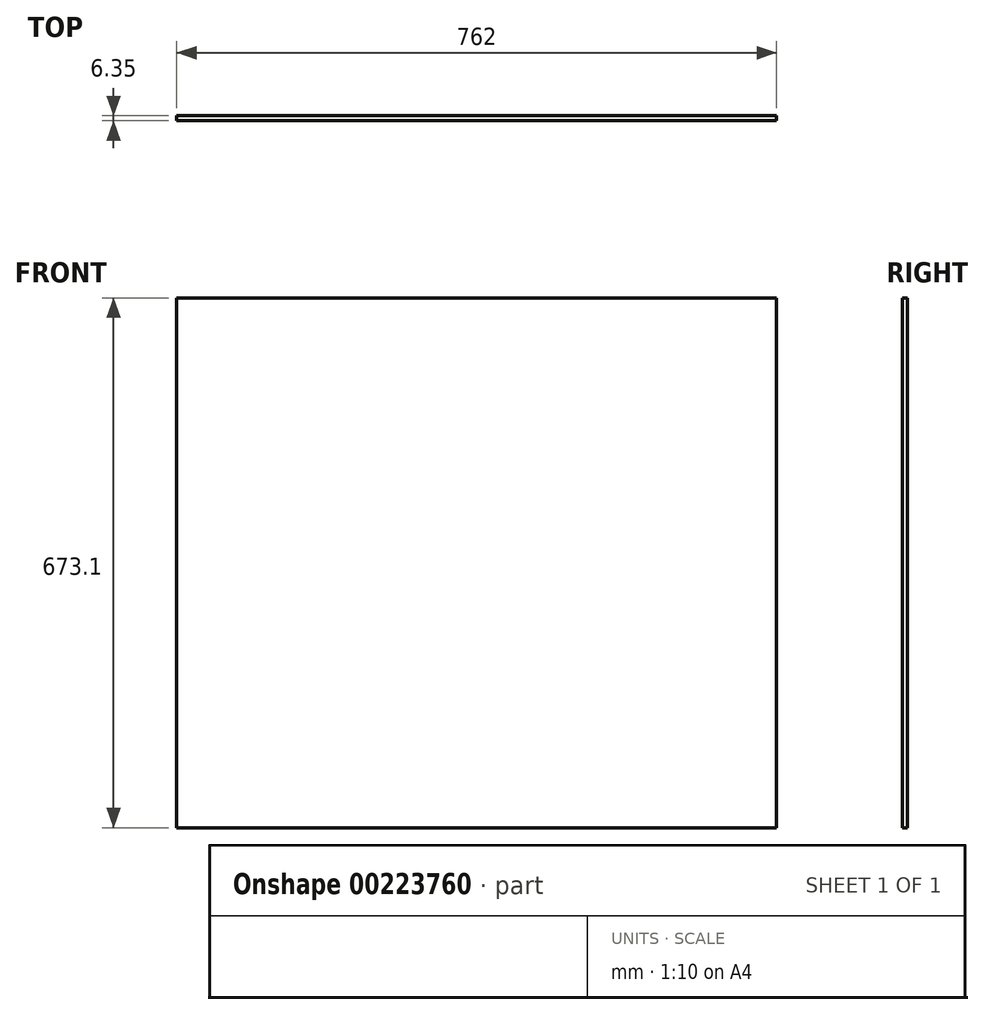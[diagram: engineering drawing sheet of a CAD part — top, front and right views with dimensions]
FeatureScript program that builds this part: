
annotation { "Feature Type Name" : "Feature", "Feature Type Description" : "" }
export const myFeature = defineFeature(function(context is Context, id is Id, definition is map)
    precondition{}
    {
        {
            var Q0;
            Q0=qCreatedBy(makeId("Front.planeOp"),FACE);
            var sketch = newSketch(context, id + "F0", { "sketchPlane" : qUnion([Q0])});
            skLineSegment(sketch, "E0.bottom", {"start": v(-723.3, -316.62) * mm, "end": v(38.7, -316.62) * mm});
            skLineSegment(sketch, "E0.top", {"start": v(-723.3, 356.48) * mm, "end": v(38.7, 356.48) * mm});
            skLineSegment(sketch, "E0.left", {"start": v(-723.3, -316.62) * mm, "end": v(-723.3, 356.48) * mm});
            skLineSegment(sketch, "E0.right", {"start": v(38.7, -316.62) * mm, "end": v(38.7, 356.48) * mm});
            skSolve(sketch);
        }
        {
            var Q0;
            Q0 = qSketchRegion(id + "F0", true);
            extrude(context, id + "F1", {"entities" : qUnion([Q0]), "oppositeDirection" : true, "depth" : 6.35 * mm});
        }
    });
